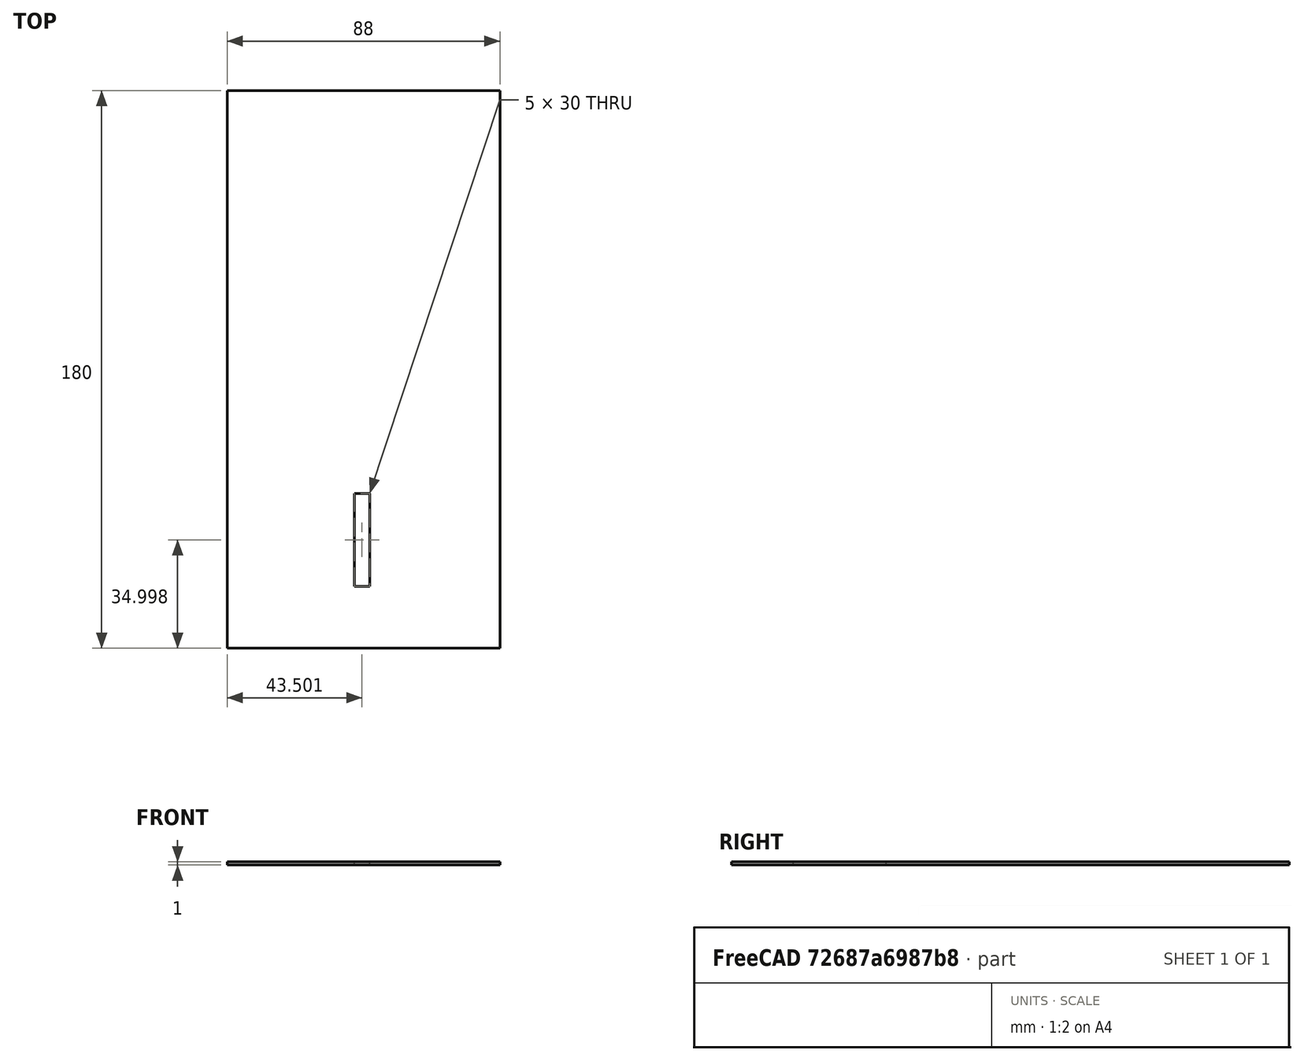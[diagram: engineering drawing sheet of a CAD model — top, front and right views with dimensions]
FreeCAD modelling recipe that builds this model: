
FCSTD DOCUMENT  (FreeCAD 0.19R24267 +148 (Git))
Label: FrontWall
License: All rights reserved
LicenseURL: http://en.wikipedia.org/wiki/All_rights_reserved
objects: Sketcher::SketchObject×1, PartDesign::Pad×1, PartDesign::Body×1
note: 4 computed .brp shape members not serialized (recipe doc carries the construction recipe); baked Part::Feature solids carry a one-line shape summary decoded from their .brp

FEATURE [Sketcher::SketchObject] Sketch002
  FullyConstrained = false
  MapMode = 5
  Support = -> [XY_Plane]
  sketch-geometry (8):
    g0: LineSegment StartX=11.661 StartY=181.378 StartZ=0 EndX=99.661 EndY=181.378 EndZ=0
    g1: LineSegment StartX=99.661 StartY=181.378 StartZ=0 EndX=99.661 EndY=1.37784 EndZ=0
    g2: LineSegment StartX=99.661 StartY=1.37784 StartZ=0 EndX=11.661 EndY=1.37784 EndZ=0
    g3: LineSegment StartX=11.661 StartY=1.37784 StartZ=0 EndX=11.661 EndY=181.378 EndZ=0
    g4: LineSegment StartX=52.661 StartY=51.3778 StartZ=0 EndX=57.661 EndY=51.3778 EndZ=0
    g5: LineSegment StartX=57.661 StartY=51.3778 StartZ=0 EndX=57.661 EndY=21.3778 EndZ=0
    g6: LineSegment StartX=57.661 StartY=21.3778 StartZ=0 EndX=52.661 EndY=21.3778 EndZ=0
    g7: LineSegment StartX=52.661 StartY=21.3778 StartZ=0 EndX=52.661 EndY=51.3778 EndZ=0
  constraints (22):
    c: Coincident(g0,g1)
    c: Coincident(g1,g2)
    c: Coincident(g2,g3)
    c: Coincident(g3,g0)
    c: Horizontal(g0)
    c: Horizontal(g2)
    c: Vertical(g1)
    c: Vertical(g3)
    c: Distance(g0) = 88
    c: Distance(g1) = 180
    c: Coincident(g4,g5)
    c: Coincident(g5,g6)
    c: Coincident(g6,g7)
    c: Coincident(g7,g4)
    c: Horizontal(g4)
    c: Horizontal(g6)
    c: Vertical(g5)
    c: Vertical(g7)
    c: Distance(g6) = 5
    c: Distance(g5) = 30
    c: Distance(g6,g2) = 20
    c: Distance(g6,g3) = 41
FEATURE [PartDesign::Pad] Pad
  Direction = (1,1,1)
  Length = 1
  Length2 = 100
  Profile = -> Sketch002
  Type = 0
FEATURE [PartDesign::Body] Body
  Group = -> [Sketch002,Pad]
  Origin = -> Origin
  Tip = -> Pad
